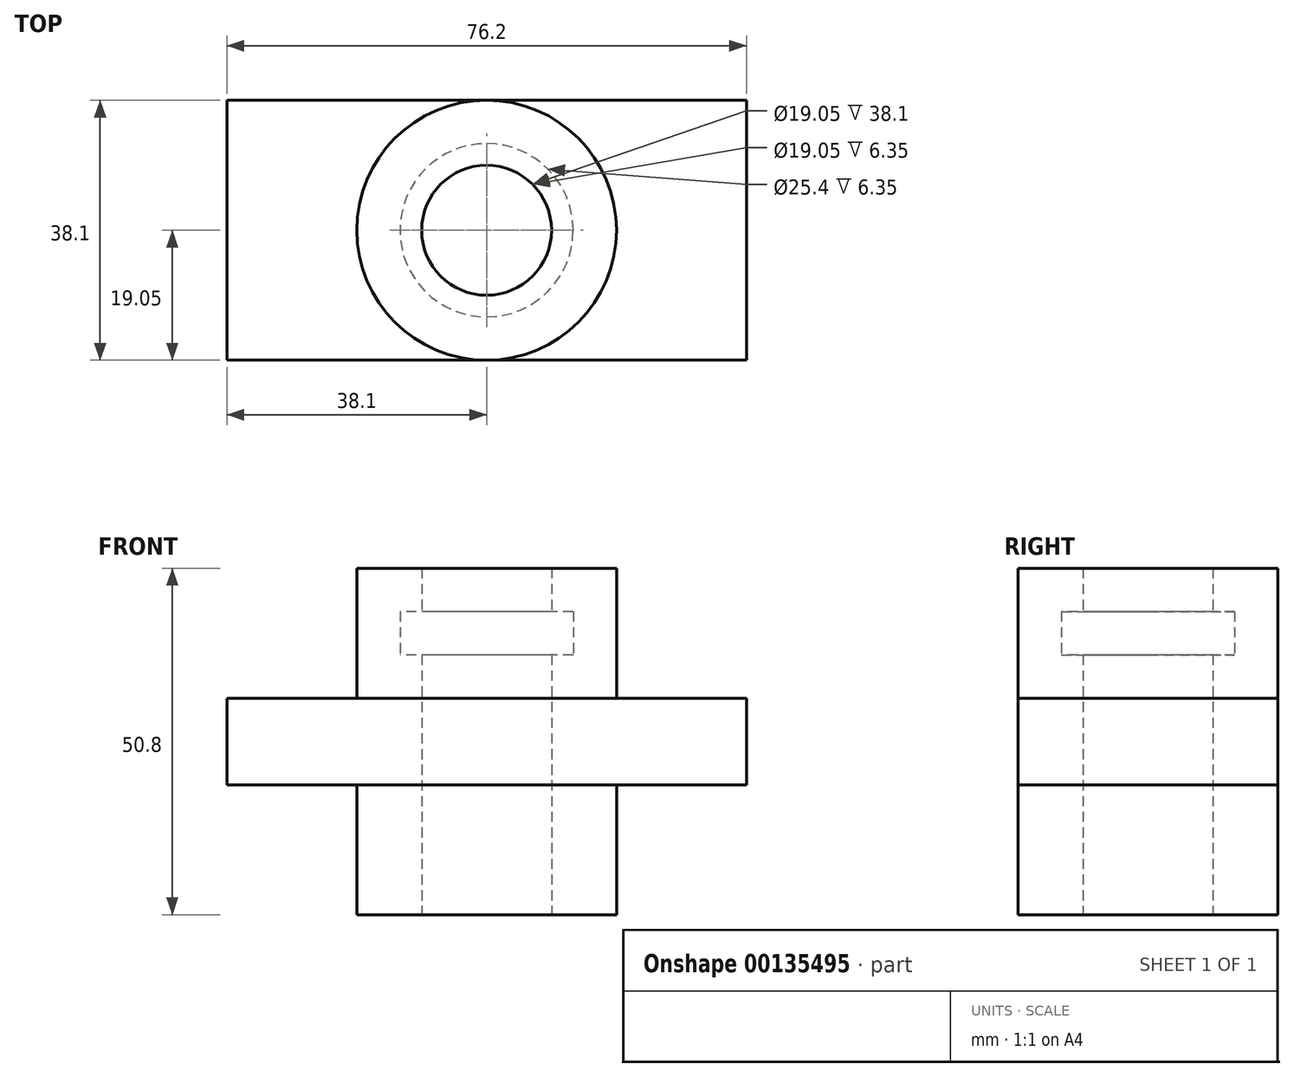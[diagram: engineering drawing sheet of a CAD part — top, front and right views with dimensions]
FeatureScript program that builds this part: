
annotation { "Feature Type Name" : "Feature", "Feature Type Description" : "" }
export const myFeature = defineFeature(function(context is Context, id is Id, definition is map)
    precondition{}
    {
        {
            var Q0;
            Q0=qCreatedBy(makeId("Top.planeOp"),FACE);
            var sketch = newSketch(context, id + "F0", { "sketchPlane" : qUnion([Q0])});
            skLineSegment(sketch, "E0.bottom", {"start": v(0, 0) * mm, "end": v(76.2, 0) * mm});
            skLineSegment(sketch, "E0.top", {"start": v(0, 38.1) * mm, "end": v(76.2, 38.1) * mm});
            skLineSegment(sketch, "E0.left", {"start": v(0, 0) * mm, "end": v(0, 38.1) * mm});
            skLineSegment(sketch, "E0.right", {"start": v(76.2, 0) * mm, "end": v(76.2, 38.1) * mm});
            skCircle(sketch, "E1", {"center": v(38.1, 19.05) * mm, "radius": 19.05 * mm});
            skCircle(sketch, "E2", {"center": v(38.1, 19.05) * mm, "radius": 9.53 * mm});
            skCircle(sketch, "E3", {"center": v(38.1, 19.05) * mm, "radius": 12.7 * mm});
            skSolve(sketch);
        }
        {
            var Q0;
            {var subQ0=sQuery(id+"F0.wireOp",EDGE,"E0.left");Q0=makeQuery(id+"F0.imprint","IMPRINT",FACE,{"disambiguationData":[TD([[makeQuery(id+"F0.imprint","IMPRINT",EDGE,{"derivedFrom":subQ0}),-1.0]])]});}
            var Q1;
            {var subQ0=sQuery(id+"F0.wireOp",EDGE,"E0.right");Q1=makeQuery(id+"F0.imprint","IMPRINT",FACE,{"disambiguationData":[TD([[makeQuery(id+"F0.imprint","IMPRINT",EDGE,{"derivedFrom":subQ0}),1.0]])]});}
            extrude(context, id + "F1", {"entities" : qUnion([Q0, Q1]), "depth" : 12.7 * mm});
        }
        {
            var Q0;
            Q0=makeQuery(id+"F0.imprint","IMPRINT",FACE,{"disambiguationData":[TD([[makeQuery(id+"F0.imprint","IMPRINT",EDGE,{"derivedFrom":sQuery(id+"F0.wireOp",EDGE,"E3")}),-1.0]])]});
            var Q1;
            Q1=makeQuery(id+"F0.imprint","IMPRINT",FACE,{"disambiguationData":[TD([[makeQuery(id+"F0.imprint","IMPRINT",EDGE,{"derivedFrom":sQuery(id+"F0.wireOp",EDGE,"E2")}),-1.0]])]});
            extrude(context, id + "F2", {"entities" : qUnion([Q0, Q1]), "operationType" : NewBodyOperationType.ADD, "depth" : 31.75 * mm, "hasSecondDirection" : true, "secondDirectionOppositeDirection" : true, "secondDirectionDepth" : 19.05 * mm});
        }
        {
            var Q0;
            Q0=makeQuery(id+"F0.imprint","IMPRINT",FACE,{"disambiguationData":[TD([[makeQuery(id+"F0.imprint","IMPRINT",EDGE,{"derivedFrom":sQuery(id+"F0.wireOp",EDGE,"E2")}),-1.0]])]});
            extrude(context, id + "F3", {"entities" : qUnion([Q0]), "operationType" : NewBodyOperationType.REMOVE, "depth" : 25.4 * mm, "hasSecondDirection" : true, "secondDirectionOppositeDirection" : false, "secondDirectionDepth" : 19.05 * mm});
        }
    });
